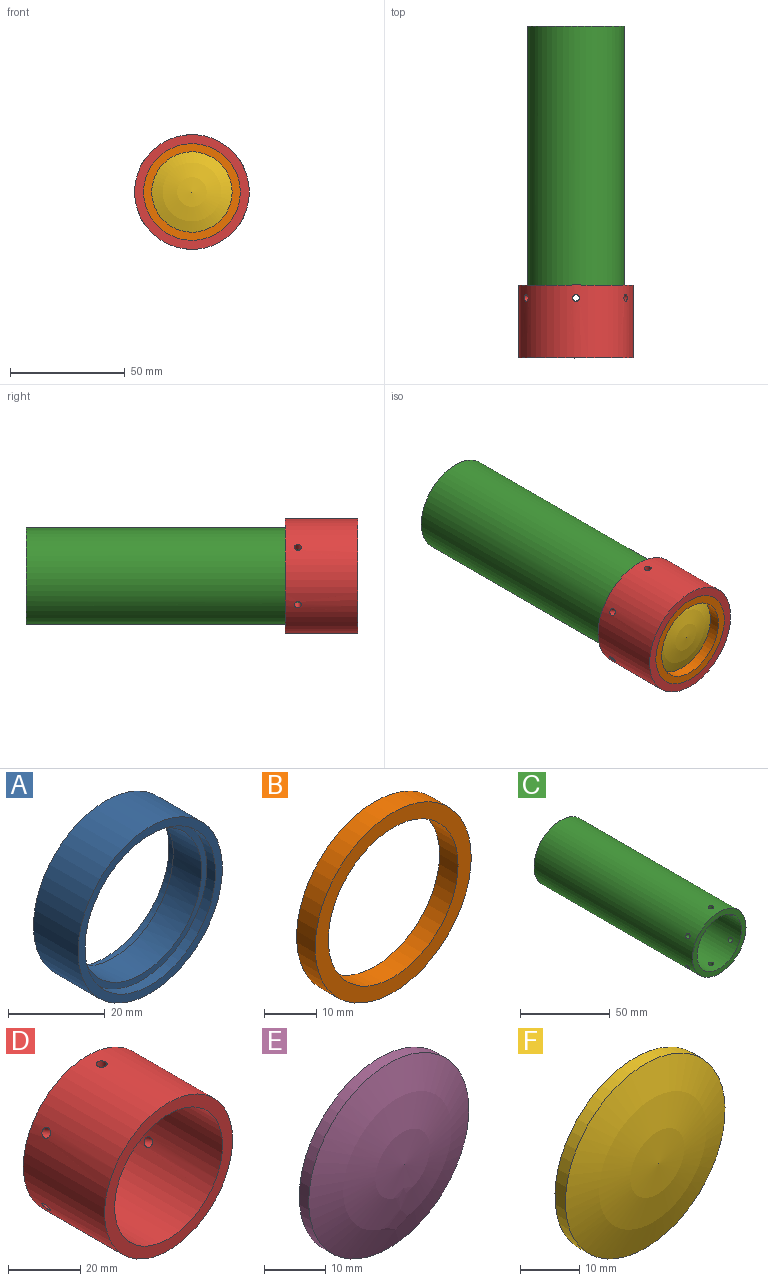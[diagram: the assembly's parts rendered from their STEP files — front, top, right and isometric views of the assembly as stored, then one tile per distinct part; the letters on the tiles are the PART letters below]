
ASSEMBLY  parts=6 mates=9
PART A: 8 faces, bbox 42.2x13x42.2 mm
  f0: cylinder r=17.53mm len=35.05mm, axis (0,1,0), area 914mm2, adj f5,f7
  f1: cylinder r=21.08mm len=42.16mm, axis (0,1,0), area 1722mm2, adj f2,f3
  f2: plane 42.16x42.16mm, normal (0,-1,0), area 256.2mm2, adj f1,f4
  f3: plane 42.16x42.16mm, normal (0,1,0), area 321.1mm2, adj f1,f6
  f4: cylinder r=19.05mm len=38.1mm, axis (0,-1,0), area 299.2mm2, adj f2,f5
  f5: plane 38.1x38.1mm, normal (0,-1,0), area 175.1mm2, adj f0,f4
  f6: cylinder r=18.5mm len=37mm, axis (0,1,0), area 255.7mm2, adj f3,f7
  f7: plane 37x37mm, normal (0,1,0), area 110.2mm2, adj f0,f6
PART B: 4 faces, bbox 42.2x5x42.2 mm
  f0: cylinder r=17.53mm len=35.05mm, axis (0,1,0), area 550.6mm2, adj f2,f3
  f1: cylinder r=21.08mm len=42.16mm, axis (0,1,0), area 662.3mm2, adj f2,f3
  f2: plane 42.16x42.16mm, normal (0,-1,0), area 431.3mm2, adj f0,f1
  f3: plane 42.16x42.16mm, normal (0,1,0), area 431.3mm2, adj f0,f1
PART C: 10 faces, bbox 42.2x124.8x42.2 mm
  f0: cylinder r=17.53mm len=124.82mm, axis (0,1,0), area 13702.2mm2, adj f2,f3,f4,f5,f6,f7,f8,f9
  f1: cylinder r=21.08mm len=124.82mm, axis (0,1,0), area 16491mm2, adj f2,f3,f4,f5,f6,f7,f8,f9
  f2: plane 42.16x42.16mm, normal (0,-1,0), area 431.3mm2, adj f0,f1
  f3: plane 42.16x42.16mm, normal (0,1,0), area 431.3mm2, adj f0,f1
  f4: cylinder r=1.5mm len=3.62mm, axis (0,0,-1), area 33.6mm2, adj f0,f1
  f5: cylinder r=1.5mm len=4.64mm, axis (0.87,0,-0.5), area 33.6mm2, adj f0,f1
  f6: cylinder r=1.5mm len=4.64mm, axis (0.87,0,0.5), area 33.6mm2, adj f0,f1
  f7: cylinder r=1.5mm len=3.62mm, axis (0,0,1), area 33.6mm2, adj f0,f1
  f8: cylinder r=1.5mm len=4.64mm, axis (-0.87,0,0.5), area 33.6mm2, adj f0,f1
  f9: cylinder r=1.5mm len=4.64mm, axis (-0.87,0,-0.5), area 33.6mm2, adj f0,f1
PART D: 10 faces, bbox 50x31.8x50 mm
  f0: cylinder r=21.08mm len=42.16mm, axis (0,1,0), area 4163.4mm2, adj f2,f3,f4,f5,f6,f7,f8,f9
  f1: cylinder r=25.01mm len=50.01mm, axis (0,1,0), area 4946.3mm2, adj f2,f3,f4,f5,f6,f7,f8,f9
  f2: plane 50.01x50.01mm, normal (0,-1,0), area 568.2mm2, adj f0,f1
  f3: plane 50.01x50.01mm, normal (0,1,0), area 568.2mm2, adj f0,f1
  f4: cylinder r=1.5mm len=3.98mm, axis (0,0,-1), area 37mm2, adj f0,f1
  f5: cylinder r=1.5mm len=4.95mm, axis (0.87,0,-0.5), area 37mm2, adj f0,f1
  f6: cylinder r=1.5mm len=4.95mm, axis (0.87,0,0.5), area 37mm2, adj f0,f1
  f7: cylinder r=1.5mm len=3.98mm, axis (0,0,1), area 37mm2, adj f0,f1
  f8: cylinder r=1.5mm len=4.95mm, axis (-0.87,0,0.5), area 37mm2, adj f0,f1
  f9: cylinder r=1.5mm len=4.95mm, axis (-0.87,0,-0.5), area 37mm2, adj f0,f1
PART E: 3 faces, bbox 37x10.4x37 mm
  f0: sphere r=49.33mm, area 1115.9mm2, adj f2
  f1: sphere r=39.5mm, area 1141.7mm2, adj f2
  f2: cylinder r=18.5mm len=37mm, axis (0,-1,0), area 255.7mm2, adj f0,f1
PART F: 3 faces, bbox 38x9x38 mm
  f0: sphere r=57.16mm, area 1167.3mm2, adj f2
  f1: sphere r=57.16mm, area 1167.3mm2, adj f2
  f2: cylinder r=19mm len=38mm, axis (0,-1,0), area 298.5mm2, adj f0,f1
PLACE A t=(0,-125.7,0)mm
PLACE B t=(0,-139.71,0)mm
PLACE C at identity fixed
PLACE D t=(0,-112.96,0)mm
PLACE E t=(0,-126.42,0)mm
PLACE F t=(0,-137.95,0)mm
MATE slider C.f0 <-> A.f0  axis (0,1,0) through (0,0,0)mm
MATE planar C.f0 <-> E.f2  axis (0,-1,0) through (0,-124.82,0)mm
MATE planar A.f0 <-> F.f2  axis (0,-1,0) through (0,-138.7,0)mm
MATE fastened D.f0 <-> B.f0  axis (0,1,0) through (0,-144.71,0)mm
MATE slider D.f0 <-> C.f0  axis (0,1,0) through (0,-144.71,0)mm
MATE slider E.f2 <-> C.f0  axis (0,-1,0) through (0,-125.32,0)mm
MATE planar A.f0 <-> C.f0  axis (0,1,0) through (0,-125.7,0)mm
MATE slider C.f0 <-> F.f2  axis (0,1,0) through (0,0,0)mm
MATE planar B.f0 <-> F.f2  axis (0,1,0) through (0,-139.71,0)mm
